# Revit family: FILTRATION ANTI-BACTERIENNE FD1000
name_source: partatom
category: Equipement de génie climatique
revit_build: Autodesk Revit 2018 (Build: 20170223_1515(x64)
units: mm (PartAtom-declared; Revit-internal decimal feet)

## family parameters
Basée sur le plan de construction = Non
Classification = Aucun
Cote de connecteur circulaire = Utiliser le diamètre
Couper avec des vides une fois chargée = Non
Partagée = Non
Point de calcul de pièce = Non
Toujours verticalement = Oui
Type d'élément = Normal

## types (1)
- FD1000
    DIAM_BOSS = 126 mm  [stored 0.413386 ft]
    EP_BRIDE = 20 mm  [stored 0.0656168 ft]
    HAUTEUR = 0 mm  [stored 0 ft]
    HAUT_BOSS = 26 mm
    HAUT_COUVERCLE = 48 mm
    HAUT_POT = 328 mm
    HAUT_TETE = 145 mm  [stored 0.475722 ft]
    LARGEUR = 0 mm  [stored 0 ft]
    LARG_TETE = 63 mm  [stored 0.206693 ft]
    LONGUEUR = 0 mm  [stored 0 ft]
    LONG_TETE = 385 mm  [stored 1.26312 ft]
    OFFSET_FLECHE = 50 mm  [stored 0.164042 ft]
    OFFSET_PERC = 63 mm  [stored 0.206693 ft]
    POIDS(Kg) = 0 mm  [stored 0 ft]
    RAY_BRIDE = 100 mm  [stored 0.328084 ft]
    RAY_ORIFICE = 39 mm  [stored 0.127953 ft]
    RAY_POT = 140 mm  [stored 0.459318 ft]
    RAY_TETE = 145 mm  [stored 0.475722 ft]
    ØBRIDE = 200 mm

note: [stored X ft] marks values corroborated as IEEE doubles in the binary element streams (Revit-internal decimal feet)

## geometry (parser evidence)
native form markers: Sweep x5
no freeform markers — native parametric forms only
